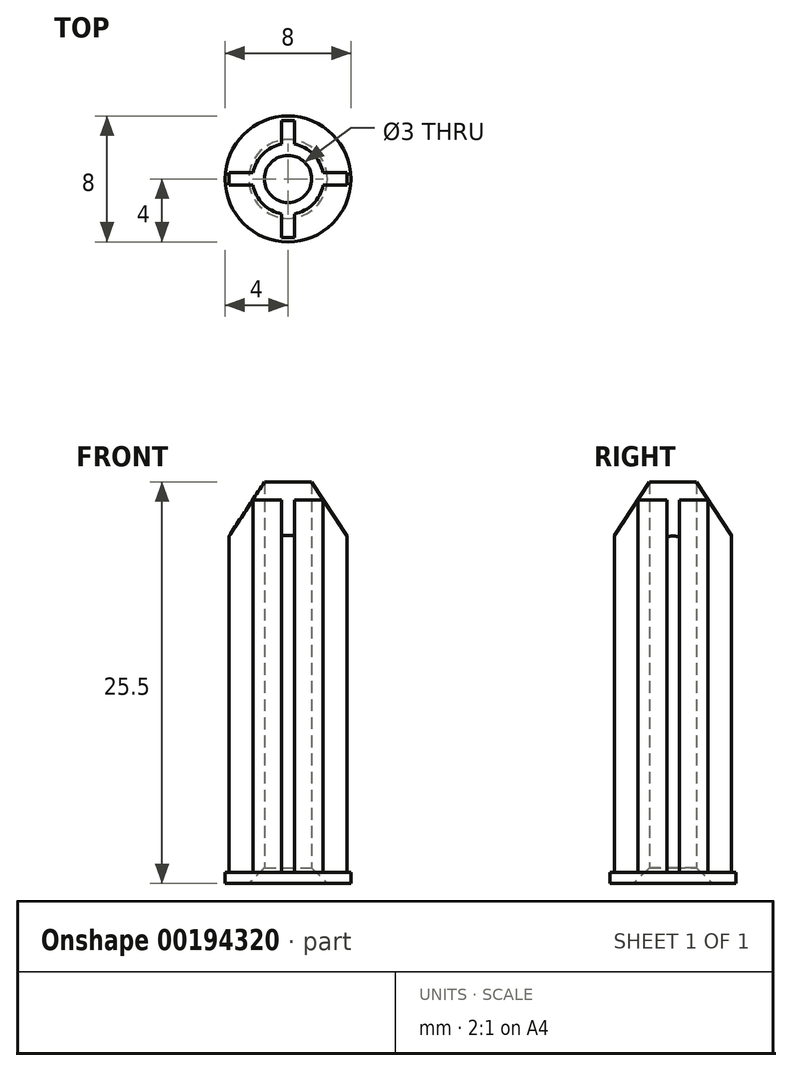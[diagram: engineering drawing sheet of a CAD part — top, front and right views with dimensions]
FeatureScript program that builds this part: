
annotation { "Feature Type Name" : "Feature", "Feature Type Description" : "" }
export const myFeature = defineFeature(function(context is Context, id is Id, definition is map)
    precondition{}
    {
        {
            var Q0;
            Q0=qCreatedBy(makeId("Top.planeOp"),FACE);
            var sketch = newSketch(context, id + "F0", { "sketchPlane" : qUnion([Q0])});
            skArc(sketch, "E0", {"start": v(2.21, 0.4) * mm, "mid": v(1.6, 1.6) * mm, "end": v(0.4, 2.21) * mm});
            skCircle(sketch, "E1", {"center": v(0, 0) * mm, "radius": 1.5 * mm});
            skLineSegment(sketch, "E2", {"start": v(2.21, -0.4) * mm, "end": v(3.75, -0.4) * mm});
            skLineSegment(sketch, "E3", {"start": v(3.75, -0.4) * mm, "end": v(3.75, 0.4) * mm});
            skLineSegment(sketch, "E4", {"start": v(3.75, 0.4) * mm, "end": v(2.21, 0.4) * mm});
            skLineSegment(sketch, "E5.MirrorCS", {"start": v(-3.75, 0.4) * mm, "end": v(-2.21, 0.4) * mm});
            skLineSegment(sketch, "E6.MirrorCS", {"start": v(-2.21, -0.4) * mm, "end": v(-3.75, -0.4) * mm});
            skLineSegment(sketch, "E7.MirrorCS", {"start": v(-3.75, -0.4) * mm, "end": v(-3.75, 0.4) * mm});
            skLineSegment(sketch, "E8.MirrorCS", {"start": v(2.21, 0.4) * mm, "end": v(3.75, 0.4) * mm});
            skLineSegment(sketch, "E9.MirrorCS", {"start": v(3.75, 0.4) * mm, "end": v(3.75, -0.4) * mm});
            skLineSegment(sketch, "E10", {"start": v(-0.4, 2.21) * mm, "end": v(-0.4, 3.71) * mm});
            skLineSegment(sketch, "E11", {"start": v(-0.4, 3.71) * mm, "end": v(0.4, 3.71) * mm});
            skLineSegment(sketch, "E12", {"start": v(0.4, 3.71) * mm, "end": v(0.4, 2.21) * mm});
            skLineSegment(sketch, "E13.MirrorCS", {"start": v(-0.4, -2.21) * mm, "end": v(-0.4, -3.71) * mm});
            skLineSegment(sketch, "E14.MirrorCS", {"start": v(0.4, -3.71) * mm, "end": v(0.4, -2.21) * mm});
            skLineSegment(sketch, "E15.MirrorCS", {"start": v(-0.4, -3.71) * mm, "end": v(0.4, -3.71) * mm});
            skArc(sketch, "E16.trimOffspring", {"start": v(-0.4, 2.21) * mm, "mid": v(-1.6, 1.6) * mm, "end": v(-2.21, 0.4) * mm});
            skArc(sketch, "E17.trimOffspring", {"start": v(-2.21, -0.4) * mm, "mid": v(-1.6, -1.6) * mm, "end": v(-0.4, -2.21) * mm});
            skArc(sketch, "E18.trimOffspring", {"start": v(0.4, -2.21) * mm, "mid": v(1.6, -1.6) * mm, "end": v(2.21, -0.4) * mm});
            skSolve(sketch);
        }
        {
            var Q0;
            Q0 = qSketchRegion(id + "F0", true);
            extrude(context, id + "F1", {"entities" : qUnion([Q0]), "depth" : 25 * mm});
        }
        {
            var Q0;
            Q0=makeQuery(id+"F1.opExtrude","CAP_FACE",FACE,{"disambiguationData":[OSD([sQuery(id+"F0.wireOp",EDGE,"E0"),sQuery(id+"F0.wireOp",EDGE,"E1"),sQuery(id+"F0.wireOp",EDGE,"E6.MirrorCS"),sQuery(id+"F0.wireOp",EDGE,"E7.MirrorCS"),sQuery(id+"F0.wireOp",EDGE,"E5.MirrorCS"),sQuery(id+"F0.wireOp",EDGE,"E8.MirrorCS"),sQuery(id+"F0.wireOp",EDGE,"E2"),sQuery(id+"F0.wireOp",EDGE,"E3"),sQuery(id+"F0.wireOp",EDGE,"E10"),sQuery(id+"F0.wireOp",EDGE,"E11"),sQuery(id+"F0.wireOp",EDGE,"E12"),sQuery(id+"F0.wireOp",EDGE,"E13.MirrorCS"),sQuery(id+"F0.wireOp",EDGE,"E14.MirrorCS"),sQuery(id+"F0.wireOp",EDGE,"E15.MirrorCS"),sQuery(id+"F0.wireOp",EDGE,"E16.trimOffspring"),sQuery(id+"F0.wireOp",EDGE,"E17.trimOffspring"),sQuery(id+"F0.wireOp",EDGE,"E18.trimOffspring")])],"isStart":true});
            var sketch = newSketch(context, id + "F2", { "sketchPlane" : qUnion([Q0])});
            skCircle(sketch, "E19.0", {"center": v(0, 0) * mm, "radius": 1.5 * mm});
            skPoint(sketch, "E20.0", {"position": v(0, 3.71) * mm});
            skCircle(sketch, "E21", {"center": v(0, 0) * mm, "radius": 4 * mm});
            skSolve(sketch);
        }
        {
            var Q0;
            Q0 = qSketchRegion(id + "F2", true);
            extrude(context, id + "F3", {"entities" : qUnion([Q0]), "operationType" : NewBodyOperationType.ADD, "depth" : 0.7 * mm});
        }
        {
            var Q0;
            Q0=makeQuery(id+"F3.opExtrude","CAP_EDGE",EDGE,{"disambiguationData":[OSD([sQuery(id+"F2.wireOp",EDGE,"E19.0")])],"isStart":false});
            chamfer(context, id + "F4", {"entities" : qUnion([Q0]), "width" : 1 * mm, "tangentPropagation" : true});
        }
        {
            var Q0;
            Q0=qCreatedBy(makeId("Right.planeOp"),FACE);
            var sketch = newSketch(context, id + "F5", { "sketchPlane" : qUnion([Q0])});
            skLineSegment(sketch, "E22", {"start": v(0, 27.1) * mm, "end": v(0, -1.85) * mm});
            skLineSegment(sketch, "E23", {"start": v(0, -1.85) * mm, "end": v(4.4, -1.8) * mm});
            skLineSegment(sketch, "E24", {"start": v(4.4, -1.8) * mm, "end": v(4.4, 20.38) * mm});
            skLineSegment(sketch, "E25", {"start": v(4.4, 20.38) * mm, "end": v(0, 27.1) * mm});
            skSolve(sketch);
        }
        {
            var Q0;
            Q0 = qSketchRegion(id + "F5", true);
            var Q1;
            Q1=sQuery(id+"F5.wireOp",EDGE,"E22");
            revolve(context, id + "F6", {"operationType" : NewBodyOperationType.INTERSECT, "entities" : qUnion([Q0]), "axis" : qUnion([Q1]), "revolveType" : RevolveType.FULL, "oppositeDirection" : true});
        }
    });
